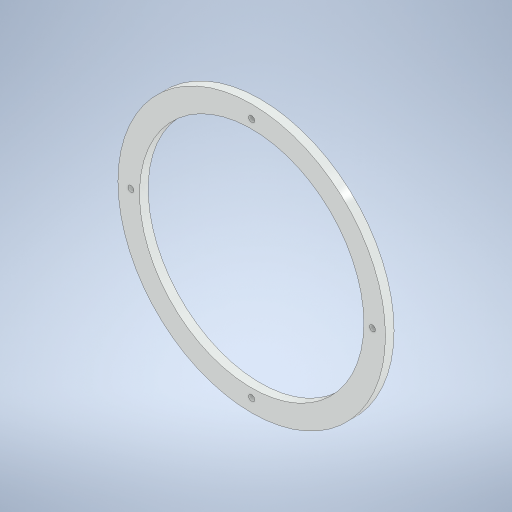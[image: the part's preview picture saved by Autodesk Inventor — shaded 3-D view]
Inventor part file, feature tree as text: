
AUTODESK INVENTOR PART (.ipt)
format: ipt  version: 2023.1 (Build 271208000, 208)  size: 257,536 bytes
history: native  units: mm
features: extrude x2, sketch x2, other x1
ambient origin geometry x8: Origin, YZ Plane, XZ Plane, XY Plane, X Axis, Y Axis, Z Axis, Center Point
bodies: Body1 (feature_tree)
feature tree (5):
  other  "솔리드1"
  extrude  "돌출1"  Depth=155.0mm
  extrude  "돌출2"  Depth=130.0mm
  sketch  "스케치1"
  sketch  "스케치2"
